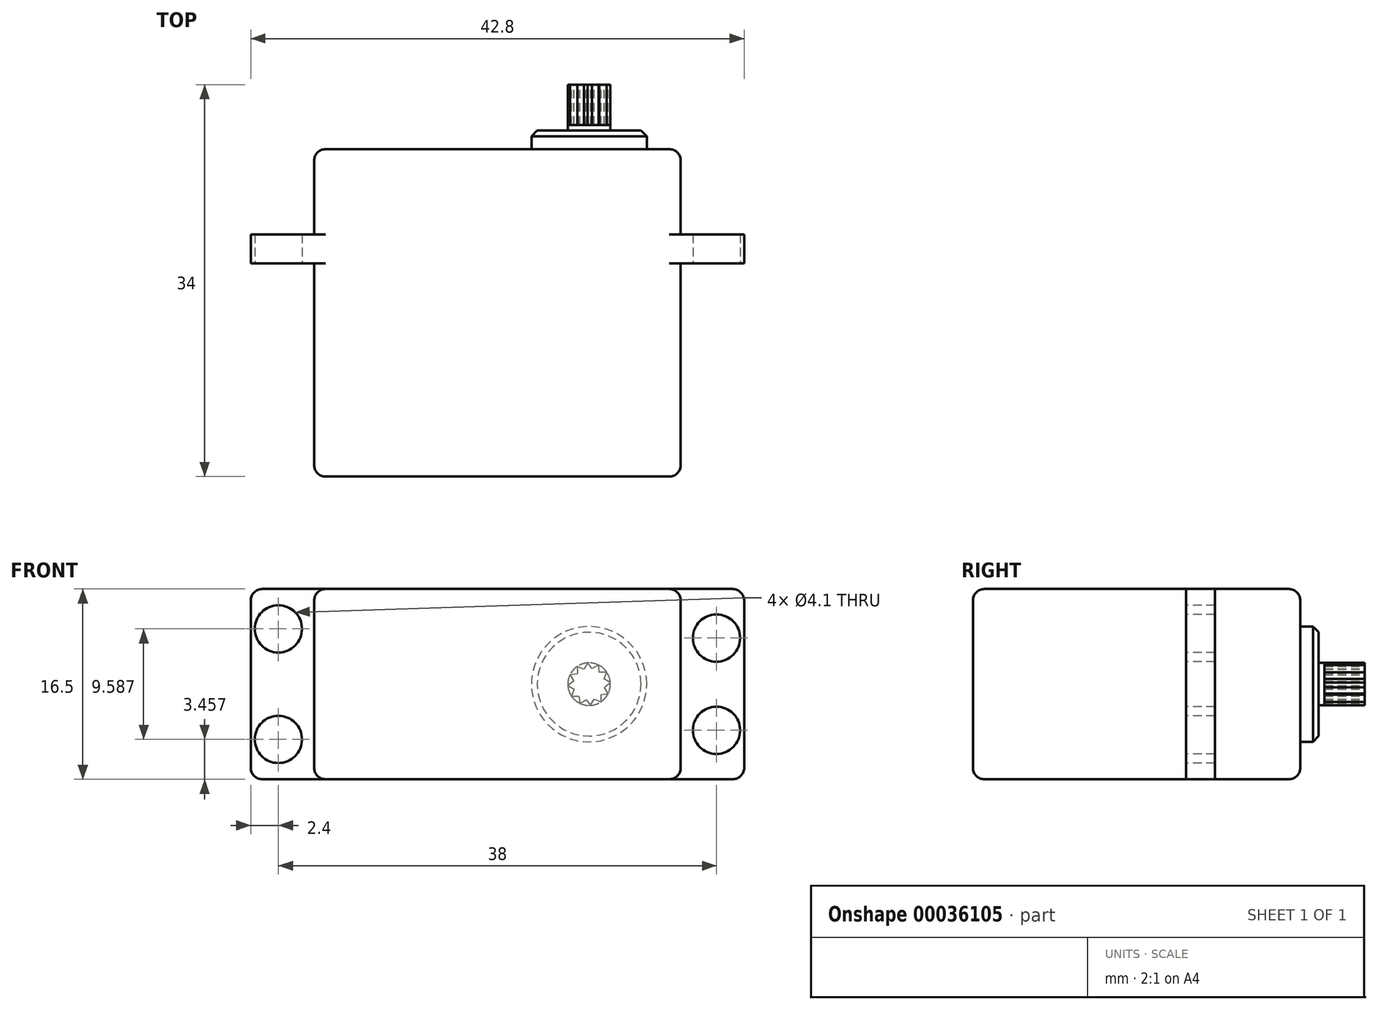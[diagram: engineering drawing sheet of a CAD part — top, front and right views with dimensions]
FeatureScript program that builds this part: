
annotation { "Feature Type Name" : "Feature", "Feature Type Description" : "" }
export const myFeature = defineFeature(function(context is Context, id is Id, definition is map)
    precondition{}
    {
        {
            var Q0;
            Q0=qCreatedBy(makeId("Top.planeOp"),FACE);
            var sketch = newSketch(context, id + "F0", { "sketchPlane" : qUnion([Q0])});
            skLineSegment(sketch, "E0.bottom", {"start": v(-15.9, 14.2) * mm, "end": v(15.9, 14.2) * mm});
            skLineSegment(sketch, "E0.top", {"start": v(-15.9, -14.2) * mm, "end": v(15.9, -14.2) * mm});
            skLineSegment(sketch, "E0.left", {"start": v(-15.9, 14.2) * mm, "end": v(-15.9, -14.2) * mm});
            skLineSegment(sketch, "E0.right", {"start": v(15.9, 14.2) * mm, "end": v(15.9, -14.2) * mm});
            skPoint(sketch, "E1", {"position": v(15.9, 0) * mm});
            skLineSegment(sketch, "E2", {"start": v(15.9, 0) * mm, "end": v(-15.9, 0) * mm, "construction": true});
            skPoint(sketch, "E3", {"position": v(0, 0) * mm});
            skLineSegment(sketch, "E4", {"start": v(-15.9, 6.8) * mm, "end": v(15.9, 6.8) * mm});
            skLineSegment(sketch, "E5", {"start": v(-15.9, 4.3) * mm, "end": v(15.9, 4.3) * mm});
            skLineSegment(sketch, "E6.left", {"start": v(-15.9, 6.8) * mm, "end": v(-15.9, 6.8) * mm});
            skLineSegment(sketch, "E7", {"start": v(-19, 4.3) * mm, "end": v(-19, 6.8) * mm, "construction": true});
            skLineSegment(sketch, "E8", {"start": v(19, 6.8) * mm, "end": v(19, 4.3) * mm, "construction": true});
            skLineSegment(sketch, "E9", {"start": v(-19, 6.8) * mm, "end": v(-21.4, 6.8) * mm});
            skLineSegment(sketch, "E10", {"start": v(-21.4, 6.8) * mm, "end": v(-21.4, 4.3) * mm});
            skLineSegment(sketch, "E11", {"start": v(-21.4, 4.3) * mm, "end": v(-19, 4.3) * mm});
            skLineSegment(sketch, "E12", {"start": v(19, 6.8) * mm, "end": v(21.4, 6.8) * mm});
            skLineSegment(sketch, "E13", {"start": v(21.4, 6.8) * mm, "end": v(21.4, 4.3) * mm});
            skLineSegment(sketch, "E14", {"start": v(21.4, 4.3) * mm, "end": v(19, 4.3) * mm});
            skLineSegment(sketch, "E15", {"start": v(-19, 6.8) * mm, "end": v(-15.9, 6.8) * mm});
            skLineSegment(sketch, "E16", {"start": v(-19, 4.3) * mm, "end": v(-15.9, 4.3) * mm});
            skLineSegment(sketch, "E17", {"start": v(15.9, 4.3) * mm, "end": v(19, 4.3) * mm});
            skLineSegment(sketch, "E18", {"start": v(15.9, 6.8) * mm, "end": v(19, 6.8) * mm});
            skSolve(sketch);
        }
        {
            var Q0;
            {var subQ2=sQuery(id+"F0.wireOp",EDGE,"E0.bottom");Q0=makeQuery(id+"F0.imprint","IMPRINT",FACE,{"disambiguationData":[TD([[makeQuery(id+"F0.imprint","IMPRINT",EDGE,{"derivedFrom":subQ2}),-1.0]])]});}
            var Q1;
            {var subQ1=sQuery(id+"F0.wireOp",EDGE,"E4");Q1=makeQuery(id+"F0.imprint","IMPRINT",FACE,{"disambiguationData":[TD([[makeQuery(id+"F0.imprint","IMPRINT",EDGE,{"derivedFrom":subQ1}),-1.0]])]});}
            var Q2;
            {var subQ2=sQuery(id+"F0.wireOp",EDGE,"E0.top");Q2=makeQuery(id+"F0.imprint","IMPRINT",FACE,{"disambiguationData":[TD([[makeQuery(id+"F0.imprint","IMPRINT",EDGE,{"derivedFrom":subQ2}),1.0]])]});}
            var Q3;
            {var subQ1=sQuery(id+"F0.wireOp",EDGE,"09e22627-e60c-491d-84b8-1f82f3b54810");Q3=makeQuery(id+"F0.imprint","IMPRINT",FACE,{"disambiguationData":[TD([[makeQuery(id+"F0.imprint","IMPRINT",EDGE,{"derivedFrom":subQ1}),1.0]])]});}
            var Q4;
            {var subQ1=sQuery(id+"F0.wireOp",EDGE,"9076f290-2de4-49c5-82f5-c9286705dbb7");Q4=makeQuery(id+"F0.imprint","IMPRINT",FACE,{"disambiguationData":[TD([[makeQuery(id+"F0.imprint","IMPRINT",EDGE,{"derivedFrom":subQ1}),-1.0]])]});}
            var Q5;
            Q5=makeQuery(id+"F0.imprint","IMPRINT",FACE,{"disambiguationData":[TD([[makeQuery(id+"F0.imprint","IMPRINT",EDGE,{"derivedFrom":sQuery(id+"F0.wireOp",EDGE,"E9")}),1.0]])]});
            var Q6;
            Q6=makeQuery(id+"F0.imprint","IMPRINT",FACE,{"disambiguationData":[TD([[makeQuery(id+"F0.imprint","IMPRINT",EDGE,{"derivedFrom":sQuery(id+"F0.wireOp",EDGE,"E12")}),-1.0]])]});
            extrude(context, id + "F1", {"entities" : qUnion([Q0, Q1, Q2, Q3, Q4, Q5, Q6]), "depth" : 16.5 * mm});
        }
        {
            var Q0;
            Q0=makeQuery(id+"F1.opExtrude","SWEPT_FACE",FACE,{"disambiguationData":[OSD([sQuery(id+"F0.wireOp",EDGE,"c4af46d5-3eda-48fc-baeb-3fe5783b968a"),sQuery(id+"F0.wireOp",EDGE,"E11")])]});
            var sketch = newSketch(context, id + "F2", { "sketchPlane" : qUnion([Q0])});
            skLineSegment(sketch, "E19.0", {"start": v(-21.4, 16.5) * mm, "end": v(-15.9, 16.5) * mm});
            skLineSegment(sketch, "E20.0", {"start": v(-19, 0) * mm, "end": v(-15.9, 0) * mm});
            skLineSegment(sketch, "E21", {"start": v(-19, 0) * mm, "end": v(-19, 16.5) * mm, "construction": true});
            skLineSegment(sketch, "E22.0", {"start": v(19, 0) * mm, "end": v(21.4, 0) * mm});
            skLineSegment(sketch, "E23.0", {"start": v(15.9, 16.5) * mm, "end": v(21.4, 16.5) * mm});
            skLineSegment(sketch, "E24", {"start": v(19, 0) * mm, "end": v(19, 16.5) * mm, "construction": true});
            skSolve(sketch);
        }
        {
            var Q0;
            {var subQ1=sQuery(id+"F0.wireOp",EDGE,"E11");Q0=makeQuery(id+"F2.imprint","IMPRINT",FACE,{"disambiguationData":[TD([[makeQuery(id+"F2.imprint","IMPRINT",EDGE,{"derivedFrom":makeQuery(id+"F1.opExtrude","SWEPT_EDGE",EDGE,{"disambiguationData":[OSD([sQuery(id+"F0.wireOp",EDGE,"E10"),subQ1])]})}),1.0]])]});}
            cPlane(context, id + "F3", {"entities" : qUnion([Q0]), "cplaneType" : CPlaneType.OFFSET, "offset" : 0 * mm, "width" : 150 * mm, "height" : 150 * mm});
        }
        {
            var Q0;
            Q0=qCreatedBy(id+"F3.planeOp",FACE);
            var sketch = newSketch(context, id + "F4", { "sketchPlane" : qUnion([Q0])});
            skLineSegment(sketch, "E25.0", {"start": v(-19, 0) * mm, "end": v(-15.9, 0) * mm});
            skPoint(sketch, "E26", {"position": v(-19, 8.25) * mm});
            skPoint(sketch, "E27", {"position": v(19, 8.25) * mm});
            skPoint(sketch, "E28.orphan", {"position": v(19, 16.5) * mm});
            skPoint(sketch, "E29.1.start.orphan", {"position": v(19, 0) * mm});
            skPoint(sketch, "E30.orphan", {"position": v(-19, 16.5) * mm});
            skPoint(sketch, "E31.0.start.orphan", {"position": v(-19, 0) * mm});
            skLineSegment(sketch, "E32", {"start": v(-19, 8.25) * mm, "end": v(-19, 13.04) * mm, "construction": true});
            skLineSegment(sketch, "E33", {"start": v(-19, 8.25) * mm, "end": v(-19, 3.46) * mm, "construction": true});
            skLineSegment(sketch, "E34", {"start": v(19, 8.25) * mm, "end": v(19, 12.25) * mm, "construction": true});
            skLineSegment(sketch, "E35", {"start": v(19, 8.25) * mm, "end": v(19, 4.25) * mm, "construction": true});
            skCircle(sketch, "E36", {"center": v(-19, 13.04) * mm, "radius": 2.05 * mm});
            skCircle(sketch, "E37", {"center": v(-19, 3.46) * mm, "radius": 2.05 * mm});
            skCircle(sketch, "E38", {"center": v(19, 12.25) * mm, "radius": 2.05 * mm});
            skCircle(sketch, "E39", {"center": v(19, 4.25) * mm, "radius": 2.05 * mm});
            skSolve(sketch);
        }
        {
            var Q0;
            Q0 = qSketchRegion(id + "F4", true);
            extrude(context, id + "F5", {"entities" : qUnion([Q0]), "operationType" : NewBodyOperationType.REMOVE, "endBound" : BoundingType.THROUGH_ALL, "oppositeDirection" : true, "depth" : 25 * mm});
        }
        {
            var Q0;
            Q0=makeQuery(id+"F1.opExtrude","SWEPT_FACE",FACE,{"disambiguationData":[OSD([sQuery(id+"F0.wireOp",EDGE,"E0.bottom")])]});
            var sketch = newSketch(context, id + "F6", { "sketchPlane" : qUnion([Q0])});
            skLineSegment(sketch, "E40", {"start": v(-15.9, 8.25) * mm, "end": v(0, 8.25) * mm, "construction": true});
            skPoint(sketch, "E41.orphan", {"position": v(15.9, 8.25) * mm});
            skPoint(sketch, "E42", {"position": v(-7.95, 8.25) * mm});
            skCircle(sketch, "E43", {"center": v(-7.95, 8.25) * mm, "radius": 5 * mm});
            skLineSegment(sketch, "E44.6", {"start": v(11.12, 7.62) * mm, "end": v(11.12, 7.62) * mm});
            skLineSegment(sketch, "E44.7", {"start": v(11.12, 7.62) * mm, "end": v(11.12, 7.62) * mm});
            skLineSegment(sketch, "E44.8", {"start": v(11.12, 7.62) * mm, "end": v(11.12, 7.62) * mm});
            skLineSegment(sketch, "E44.9", {"start": v(11.12, 7.62) * mm, "end": v(11.12, 7.62) * mm});
            skLineSegment(sketch, "E44.10", {"start": v(11.12, 7.62) * mm, "end": v(11.12, 7.62) * mm});
            skLineSegment(sketch, "E44.11", {"start": v(11.12, 7.62) * mm, "end": v(11.12, 7.62) * mm});
            skLineSegment(sketch, "E44.12", {"start": v(11.12, 7.62) * mm, "end": v(11.12, 7.62) * mm});
            skLineSegment(sketch, "E44.13", {"start": v(11.12, 7.62) * mm, "end": v(11.12, 7.62) * mm});
            skLineSegment(sketch, "E44.14", {"start": v(11.12, 7.62) * mm, "end": v(11.12, 7.62) * mm});
            skLineSegment(sketch, "E44.15", {"start": v(11.12, 7.62) * mm, "end": v(11.12, 7.62) * mm});
            skLineSegment(sketch, "E44.16", {"start": v(11.12, 7.62) * mm, "end": v(11.12, 7.62) * mm});
            skLineSegment(sketch, "E44.17", {"start": v(11.12, 7.62) * mm, "end": v(11.12, 7.62) * mm});
            skLineSegment(sketch, "E44.18", {"start": v(11.12, 7.62) * mm, "end": v(11.12, 7.62) * mm});
            skLineSegment(sketch, "E44.19", {"start": v(11.12, 7.62) * mm, "end": v(11.12, 7.62) * mm});
            skCircle(sketch, "E45", {"center": v(-7.95, 8.25) * mm, "radius": 1.85 * mm});
            skSolve(sketch);
        }
        {
            var Q0;
            Q0=makeQuery(id+"F6.imprint","IMPRINT",FACE,{"disambiguationData":[TD([[makeQuery(id+"F6.imprint","IMPRINT",EDGE,{"derivedFrom":sQuery(id+"F6.wireOp",EDGE,"E43")}),1.0]])]});
            var Q1;
            Q1=makeQuery(id+"F6.imprint","IMPRINT",FACE,{"disambiguationData":[TD([[makeQuery(id+"F6.imprint","IMPRINT",EDGE,{"derivedFrom":sQuery(id+"F6.wireOp",EDGE,"E45")}),1.0]])]});
            var Q2;
            Q2=sQuery(id+"F6.wireOp",EDGE,"E43");
            extrude(context, id + "F7", {"entities" : qUnion([Q0, Q1]), "operationType" : NewBodyOperationType.ADD, "surfaceEntities" : qUnion([Q2]), "depth" : 1.6 * mm});
        }
        {
            var Q0;
            Q0=makeQuery(id+"F7.opExtrude","CAP_EDGE",EDGE,{"disambiguationData":[OSD([sQuery(id+"F6.wireOp",EDGE,"E43")])],"isStart":false});
            chamfer(context, id + "F8", {"entities" : qUnion([Q0]), "width" : 0.5 * mm, "tangentPropagation" : true});
        }
        {
            var Q0;
            Q0=makeQuery(id+"F7.opExtrude","CAP_FACE",FACE,{"disambiguationData":[OSD([sQuery(id+"F6.wireOp",EDGE,"E43")])],"isStart":false});
            var sketch = newSketch(context, id + "F9", { "sketchPlane" : qUnion([Q0])});
            skCircle(sketch, "E46.0", {"center": v(-7.95, 8.25) * mm, "radius": 1.85 * mm});
            skSolve(sketch);
        }
        {
            var Q0;
            Q0=makeQuery(id+"F9.imprint","IMPRINT",FACE,{"disambiguationData":[TD([[makeQuery(id+"F9.imprint","IMPRINT",EDGE,{"derivedFrom":sQuery(id+"F9.wireOp",EDGE,"E46.0")}),1.0]])]});
            extrude(context, id + "F10", {"entities" : qUnion([Q0]), "depth" : 4 * mm});
        }
        {
            var Q0;
            Q0=makeQuery(id+"F10.opExtrude","CAP_FACE",FACE,{"disambiguationData":[OSD([sQuery(id+"F9.wireOp",EDGE,"E46.0")])],"isStart":false});
            var sketch = newSketch(context, id + "F11", { "sketchPlane" : qUnion([Q0])});
            skCircle(sketch, "E47", {"center": v(-7.95, 8.25) * mm, "radius": 1.37 * mm});
            skLineSegment(sketch, "E48", {"start": v(-7.82, 10.1) * mm, "end": v(-7.5, 9.54) * mm});
            skLineSegment(sketch, "E49", {"start": v(-7.5, 9.54) * mm, "end": v(-6.92, 9.78) * mm});
            skLineSegment(sketch, "E50", {"start": v(-6.92, 9.78) * mm, "end": v(-6.92, 9.15) * mm});
            skLineSegment(sketch, "E51", {"start": v(-6.92, 9.15) * mm, "end": v(-6.3, 9.06) * mm});
            skLineSegment(sketch, "E52", {"start": v(-6.3, 9.06) * mm, "end": v(-6.6, 8.51) * mm});
            skLineSegment(sketch, "E53", {"start": v(-6.6, 8.51) * mm, "end": v(-6.1, 8.12) * mm});
            skLineSegment(sketch, "E54", {"start": v(-6.1, 8.12) * mm, "end": v(-6.66, 7.8) * mm});
            skLineSegment(sketch, "E55", {"start": v(-6.66, 7.8) * mm, "end": v(-6.42, 7.22) * mm});
            skLineSegment(sketch, "E56", {"start": v(-6.42, 7.22) * mm, "end": v(-7.05, 7.22) * mm});
            skLineSegment(sketch, "E57", {"start": v(-7.05, 7.22) * mm, "end": v(-7.14, 6.6) * mm});
            skLineSegment(sketch, "E58", {"start": v(-7.14, 6.6) * mm, "end": v(-7.69, 6.9) * mm});
            skLineSegment(sketch, "E59", {"start": v(-7.69, 6.9) * mm, "end": v(-8.08, 6.4) * mm});
            skLineSegment(sketch, "E60", {"start": v(-8.08, 6.4) * mm, "end": v(-8.4, 6.96) * mm});
            skLineSegment(sketch, "E61", {"start": v(-8.4, 6.96) * mm, "end": v(-8.98, 6.72) * mm});
            skLineSegment(sketch, "E62", {"start": v(-8.98, 6.72) * mm, "end": v(-8.98, 7.35) * mm});
            skLineSegment(sketch, "E63", {"start": v(-8.98, 7.35) * mm, "end": v(-9.6, 7.44) * mm});
            skLineSegment(sketch, "E64", {"start": v(-9.6, 7.44) * mm, "end": v(-9.3, 7.99) * mm});
            skLineSegment(sketch, "E65", {"start": v(-9.3, 7.99) * mm, "end": v(-9.8, 8.38) * mm});
            skLineSegment(sketch, "E66", {"start": v(-9.48, 9.28) * mm, "end": v(-8.85, 9.28) * mm});
            skLineSegment(sketch, "E67", {"start": v(-8.85, 9.28) * mm, "end": v(-8.76, 9.9) * mm});
            skLineSegment(sketch, "E68", {"start": v(-8.76, 9.9) * mm, "end": v(-8.21, 9.6) * mm});
            skLineSegment(sketch, "E69", {"start": v(-8.21, 9.6) * mm, "end": v(-7.82, 10.1) * mm});
            skLineSegment(sketch, "E70", {"start": v(-9.8, 8.38) * mm, "end": v(-9.24, 8.7) * mm});
            skLineSegment(sketch, "E71", {"start": v(-9.24, 8.7) * mm, "end": v(-9.48, 9.28) * mm});
            skSolve(sketch);
        }
        {
            var Q0;
            {var subQ2=sQuery(id+"F11.wireOp",EDGE,"E66");Q0=makeQuery(id+"F11.imprint","IMPRINT",FACE,{"disambiguationData":[TD([[makeQuery(id+"F11.imprint","IMPRINT",EDGE,{"derivedFrom":subQ2}),1.0]])]});}
            var Q1;
            {var subQ2=sQuery(id+"F11.wireOp",EDGE,"E70");Q1=makeQuery(id+"F11.imprint","IMPRINT",FACE,{"disambiguationData":[TD([[makeQuery(id+"F11.imprint","IMPRINT",EDGE,{"derivedFrom":subQ2}),1.0]])]});}
            var Q2;
            {var subQ2=sQuery(id+"F11.wireOp",EDGE,"E64");Q2=makeQuery(id+"F11.imprint","IMPRINT",FACE,{"disambiguationData":[TD([[makeQuery(id+"F11.imprint","IMPRINT",EDGE,{"derivedFrom":subQ2}),1.0]])]});}
            var Q3;
            {var subQ2=sQuery(id+"F11.wireOp",EDGE,"E62");Q3=makeQuery(id+"F11.imprint","IMPRINT",FACE,{"disambiguationData":[TD([[makeQuery(id+"F11.imprint","IMPRINT",EDGE,{"derivedFrom":subQ2}),1.0]])]});}
            var Q4;
            {var subQ2=sQuery(id+"F11.wireOp",EDGE,"E60");Q4=makeQuery(id+"F11.imprint","IMPRINT",FACE,{"disambiguationData":[TD([[makeQuery(id+"F11.imprint","IMPRINT",EDGE,{"derivedFrom":subQ2}),1.0]])]});}
            var Q5;
            {var subQ2=sQuery(id+"F11.wireOp",EDGE,"E58");Q5=makeQuery(id+"F11.imprint","IMPRINT",FACE,{"disambiguationData":[TD([[makeQuery(id+"F11.imprint","IMPRINT",EDGE,{"derivedFrom":subQ2}),1.0]])]});}
            var Q6;
            {var subQ2=sQuery(id+"F11.wireOp",EDGE,"E56");Q6=makeQuery(id+"F11.imprint","IMPRINT",FACE,{"disambiguationData":[TD([[makeQuery(id+"F11.imprint","IMPRINT",EDGE,{"derivedFrom":subQ2}),1.0]])]});}
            var Q7;
            {var subQ2=sQuery(id+"F11.wireOp",EDGE,"E54");Q7=makeQuery(id+"F11.imprint","IMPRINT",FACE,{"disambiguationData":[TD([[makeQuery(id+"F11.imprint","IMPRINT",EDGE,{"derivedFrom":subQ2}),1.0]])]});}
            var Q8;
            {var subQ2=sQuery(id+"F11.wireOp",EDGE,"E52");Q8=makeQuery(id+"F11.imprint","IMPRINT",FACE,{"disambiguationData":[TD([[makeQuery(id+"F11.imprint","IMPRINT",EDGE,{"derivedFrom":subQ2}),1.0]])]});}
            var Q9;
            {var subQ2=sQuery(id+"F11.wireOp",EDGE,"E50");Q9=makeQuery(id+"F11.imprint","IMPRINT",FACE,{"disambiguationData":[TD([[makeQuery(id+"F11.imprint","IMPRINT",EDGE,{"derivedFrom":subQ2}),1.0]])]});}
            var Q10;
            {var subQ2=sQuery(id+"F11.wireOp",EDGE,"E48");Q10=makeQuery(id+"F11.imprint","IMPRINT",FACE,{"disambiguationData":[TD([[makeQuery(id+"F11.imprint","IMPRINT",EDGE,{"derivedFrom":subQ2}),1.0]])]});}
            var Q11;
            {var subQ1=sQuery(id+"F11.wireOp",EDGE,"E68");Q11=makeQuery(id+"F11.imprint","IMPRINT",FACE,{"disambiguationData":[TD([[makeQuery(id+"F11.imprint","IMPRINT",EDGE,{"derivedFrom":subQ1}),1.0]])]});}
            extrude(context, id + "F12", {"entities" : qUnion([Q0, Q1, Q2, Q3, Q4, Q5, Q6, Q7, Q8, Q9, Q10, Q11]), "operationType" : NewBodyOperationType.REMOVE, "oppositeDirection" : true, "depth" : 3.5 * mm});
        }
        {
            var Q0;
            Q0=makeQuery(id+"F1.opExtrude","SWEPT_FACE",FACE,{"disambiguationData":[OSD([sQuery(id+"F0.wireOp",EDGE,"E0.top")])]});
            var Q1;
            Q1=makeQuery(id+"F1.opExtrude","CAP_EDGE",EDGE,{"disambiguationData":[OSD([sQuery(id+"F0.wireOp",EDGE,"E0.bottom")])],"isStart":false});
            var Q2;
            {var subQ0=sQuery(id+"F0.wireOp",EDGE,"E0.right");Q2=makeQuery(id+"F1.opExtrude","CAP_EDGE",EDGE,{"disambiguationData":[OSD([subQ0]),TDD([makeQuery(id+"F0.imprint","IMPRINT",EDGE,{"disambiguationData":[TD([[makeQuery(id+"F0.imprint","INTERSECT",VERTEX,{"derivedFrom":[sQuery(id+"F0.wireOp",EDGE,"E0.top"),subQ0]}),1.0]])],"derivedFrom":subQ0})])],"isStart":false});}
            var Q3;
            {var subQ0=sQuery(id+"F0.wireOp",EDGE,"E0.right");Q3=makeQuery(id+"F1.opExtrude","CAP_EDGE",EDGE,{"disambiguationData":[OSD([subQ0]),TDD([makeQuery(id+"F0.imprint","IMPRINT",EDGE,{"disambiguationData":[TD([[makeQuery(id+"F0.imprint","INTERSECT",VERTEX,{"derivedFrom":[sQuery(id+"F0.wireOp",EDGE,"E0.top"),subQ0]}),1.0]])],"derivedFrom":subQ0})])],"isStart":true});}
            var Q4;
            {var subQ0=sQuery(id+"F0.wireOp",EDGE,"E0.left");Q4=makeQuery(id+"F1.opExtrude","CAP_EDGE",EDGE,{"disambiguationData":[OSD([subQ0]),TDD([makeQuery(id+"F0.imprint","IMPRINT",EDGE,{"disambiguationData":[TD([[makeQuery(id+"F0.imprint","INTERSECT",VERTEX,{"derivedFrom":[sQuery(id+"F0.wireOp",EDGE,"E0.top"),subQ0]}),1.0]])],"derivedFrom":subQ0})])],"isStart":true});}
            var Q5;
            {var subQ0=sQuery(id+"F0.wireOp",EDGE,"E0.left");Q5=makeQuery(id+"F1.opExtrude","CAP_EDGE",EDGE,{"disambiguationData":[OSD([subQ0]),TDD([makeQuery(id+"F0.imprint","IMPRINT",EDGE,{"disambiguationData":[TD([[makeQuery(id+"F0.imprint","INTERSECT",VERTEX,{"derivedFrom":[sQuery(id+"F0.wireOp",EDGE,"E0.top"),subQ0]}),1.0]])],"derivedFrom":subQ0})])],"isStart":false});}
            var Q6;
            Q6=makeQuery(id+"F1.opExtrude","SWEPT_EDGE",EDGE,{"disambiguationData":[OSD([sQuery(id+"F0.wireOp",EDGE,"E0.bottom"),sQuery(id+"F0.wireOp",EDGE,"E0.left")])]});
            var Q7;
            Q7=makeQuery(id+"F1.opExtrude","CAP_EDGE",EDGE,{"disambiguationData":[OSD([sQuery(id+"F0.wireOp",EDGE,"E0.bottom")])],"isStart":true});
            var Q8;
            {var subQ0=sQuery(id+"F0.wireOp",EDGE,"E0.right");Q8=makeQuery(id+"F1.opExtrude","CAP_EDGE",EDGE,{"disambiguationData":[OSD([subQ0]),TDD([makeQuery(id+"F0.imprint","IMPRINT",EDGE,{"disambiguationData":[TD([[makeQuery(id+"F0.imprint","INTERSECT",VERTEX,{"derivedFrom":[sQuery(id+"F0.wireOp",EDGE,"E0.bottom"),subQ0]}),-1.0]])],"derivedFrom":subQ0})])],"isStart":true});}
            var Q9;
            {var subQ0=sQuery(id+"F0.wireOp",EDGE,"E0.right");Q9=makeQuery(id+"F1.opExtrude","CAP_EDGE",EDGE,{"disambiguationData":[OSD([subQ0]),TDD([makeQuery(id+"F0.imprint","IMPRINT",EDGE,{"disambiguationData":[TD([[makeQuery(id+"F0.imprint","INTERSECT",VERTEX,{"derivedFrom":[sQuery(id+"F0.wireOp",EDGE,"E0.bottom"),subQ0]}),-1.0]])],"derivedFrom":subQ0})])],"isStart":false});}
            var Q10;
            Q10=makeQuery(id+"F1.opExtrude","CAP_EDGE",EDGE,{"disambiguationData":[OSD([sQuery(id+"F0.wireOp",EDGE,"E13")])],"isStart":false});
            var Q11;
            Q11=makeQuery(id+"F1.opExtrude","CAP_EDGE",EDGE,{"disambiguationData":[OSD([sQuery(id+"F0.wireOp",EDGE,"E13")])],"isStart":true});
            var Q12;
            Q12=makeQuery(id+"F1.opExtrude","CAP_EDGE",EDGE,{"disambiguationData":[OSD([sQuery(id+"F0.wireOp",EDGE,"E10")])],"isStart":true});
            var Q13;
            Q13=makeQuery(id+"F1.opExtrude","CAP_EDGE",EDGE,{"disambiguationData":[OSD([sQuery(id+"F0.wireOp",EDGE,"E10")])],"isStart":false});
            var Q14;
            {var subQ0=sQuery(id+"F0.wireOp",EDGE,"E0.left");Q14=makeQuery(id+"F1.opExtrude","CAP_EDGE",EDGE,{"disambiguationData":[OSD([subQ0]),TDD([makeQuery(id+"F0.imprint","IMPRINT",EDGE,{"disambiguationData":[TD([[makeQuery(id+"F0.imprint","INTERSECT",VERTEX,{"derivedFrom":[sQuery(id+"F0.wireOp",EDGE,"E0.bottom"),subQ0]}),-1.0]])],"derivedFrom":subQ0})])],"isStart":false});}
            var Q15;
            {var subQ0=sQuery(id+"F0.wireOp",EDGE,"E0.left");Q15=makeQuery(id+"F1.opExtrude","CAP_EDGE",EDGE,{"disambiguationData":[OSD([subQ0]),TDD([makeQuery(id+"F0.imprint","IMPRINT",EDGE,{"disambiguationData":[TD([[makeQuery(id+"F0.imprint","INTERSECT",VERTEX,{"derivedFrom":[sQuery(id+"F0.wireOp",EDGE,"E0.bottom"),subQ0]}),-1.0]])],"derivedFrom":subQ0})])],"isStart":true});}
            var Q16;
            Q16=makeQuery(id+"F1.opExtrude","SWEPT_EDGE",EDGE,{"disambiguationData":[OSD([sQuery(id+"F0.wireOp",EDGE,"E0.bottom"),sQuery(id+"F0.wireOp",EDGE,"E0.right")])]});
            fillet(context, id + "F13", {"entities" : qUnion([Q0, Q1, Q2, Q3, Q4, Q5, Q6, Q7, Q8, Q9, Q10, Q11, Q12, Q13, Q14, Q15, Q16]), "radius" : 1 * mm, "allowEdgeOverflow" : false});
        }
    });
